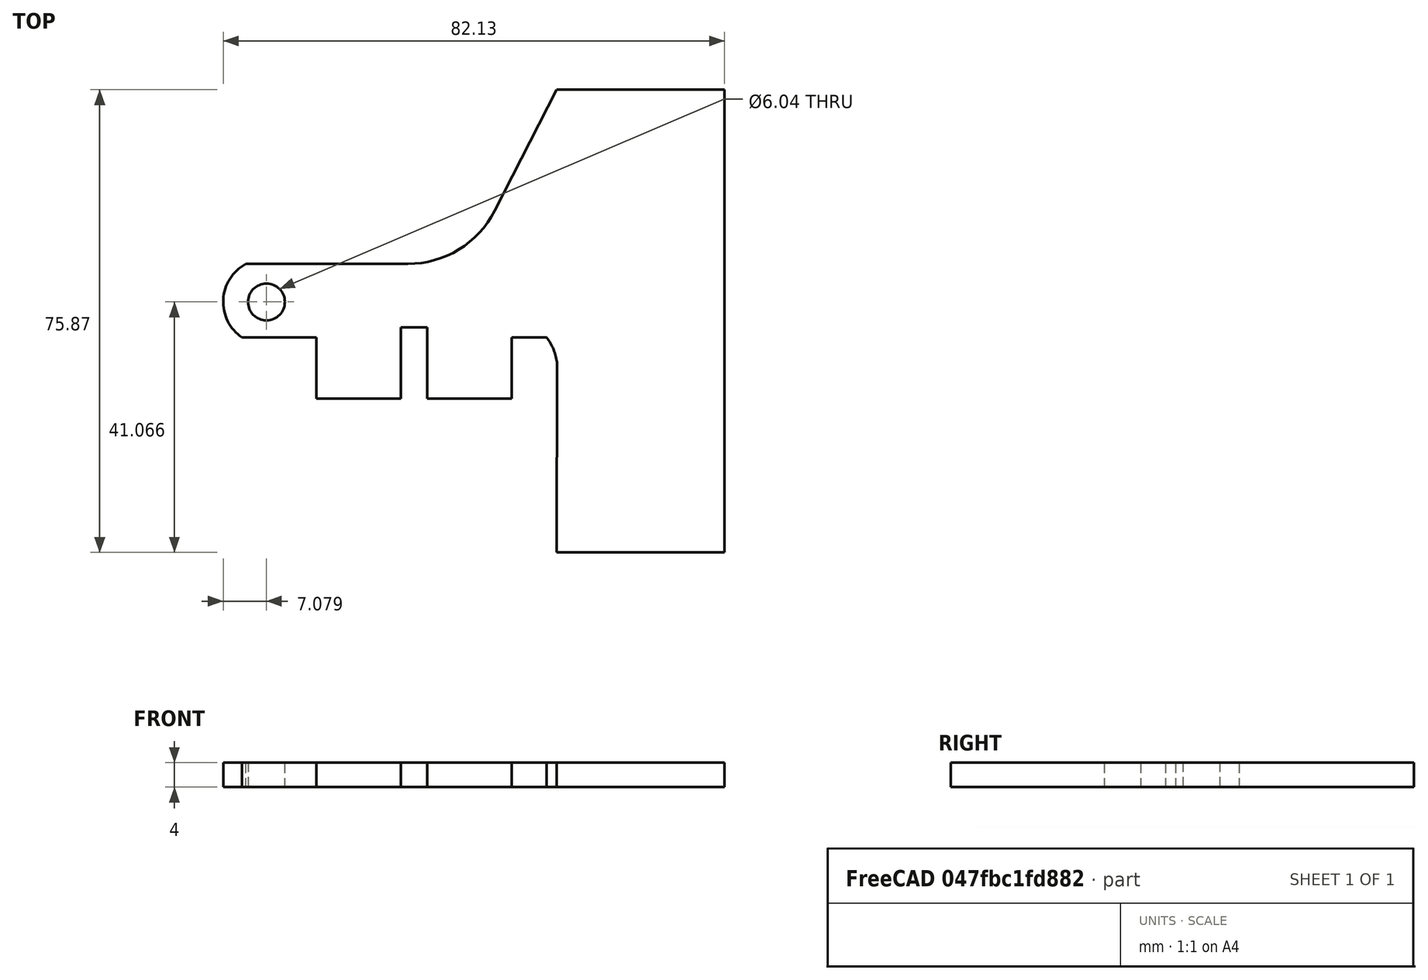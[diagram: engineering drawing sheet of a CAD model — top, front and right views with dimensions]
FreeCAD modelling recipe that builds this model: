
FCSTD DOCUMENT  (FreeCAD 0.18R16131 (Git))
Label: solo_banderuola4mm_v3
License: All rights reserved
LicenseURL: http://en.wikipedia.org/wiki/All_rights_reserved
objects: Sketcher::SketchObject×1, PartDesign::Pad×1, PartDesign::Body×1
note: 4 computed .brp shape members not serialized (recipe doc carries the construction recipe); baked Part::Feature solids carry a one-line shape summary decoded from their .brp

FEATURE [Sketcher::SketchObject] CopySketch004
  sketch-geometry (24):
    g0: LineSegment StartX=-27.5345 StartY=12.0853 StartZ=0 EndX=-1.01073 EndY=12.0853 EndZ=0
    g1: LineSegment StartX=13.2094 StartY=20.7802 StartZ=0 EndX=23.3838 EndY=40.6518 EndZ=0
    g2: LineSegment StartX=23.3838 StartY=40.6518 StartZ=0 EndX=50.8604 EndY=40.6518 EndZ=0
    g3: LineSegment StartX=50.8604 StartY=40.6518 StartZ=0 EndX=50.8604 EndY=0 EndZ=0
    g4: ArcOfCircle CenterX=-1.01073 CenterY=28.061 CenterZ=0 NormalX=0 NormalY=0 NormalZ=1 AngleXU=0 Radius=15.9757 StartAngle=4.71239 EndAngle=5.80998
    g5: GeomPoint X=16 Y=0 Z=0
    g6: GeomPoint X=-16 Y=-9e-16 Z=0
    g7: LineSegment StartX=-16 StartY=-9e-16 StartZ=0 EndX=-16 EndY=-10 EndZ=0
    g8: LineSegment StartX=-16 StartY=-10 StartZ=0 EndX=-2.15 EndY=-10 EndZ=0
    g9: LineSegment StartX=16 StartY=-10 StartZ=0 EndX=16 EndY=0 EndZ=0
    g10: GeomPoint X=-2.15 Y=-10 Z=0
    g11: GeomPoint X=2.15 Y=-10 Z=0
    g12: LineSegment StartX=-2.15 StartY=-10 StartZ=0 EndX=-2.15 EndY=1.64739 EndZ=0
    g13: LineSegment StartX=-2.15 StartY=1.64739 StartZ=0 EndX=2.15 EndY=1.64739 EndZ=0
    g14: LineSegment StartX=2.15 StartY=1.64739 StartZ=0 EndX=2.15 EndY=-10 EndZ=0
    g15: LineSegment StartX=2.15 StartY=-10 StartZ=0 EndX=16 EndY=-10 EndZ=0
    g16: ArcOfCircle CenterX=15.5785 CenterY=-4.94395 CenterZ=0 NormalX=0 NormalY=0 NormalZ=1 AngleXU=0 Radius=7.87288 StartAngle=0.112427 EndAngle=0.678944
    g17: LineSegment StartX=23.4017 StartY=-4.06069 StartZ=0 EndX=23.3838 EndY=-35.221 EndZ=0
    g18: LineSegment StartX=23.3838 StartY=-35.221 StartZ=0 EndX=50.8604 EndY=-35.221 EndZ=0
    g19: LineSegment StartX=50.8604 StartY=-35.221 StartZ=0 EndX=50.8604 EndY=0 EndZ=0
    g20: LineSegment StartX=16 StartY=0 StartZ=0 EndX=21.7055 EndY=0 EndZ=0
    g21: LineSegment StartX=-16 StartY=-9e-16 StartZ=0 EndX=-28.1836 EndY=-9e-16 EndZ=0
    g22: Circle CenterX=-24.1906 CenterY=5.84561 CenterZ=0 NormalX=0 NormalY=0 NormalZ=1 AngleXU=0 Radius=3.02
    g23: ArcOfCircle CenterX=-24.1906 CenterY=5.84561 CenterZ=0 NormalX=0 NormalY=0 NormalZ=1 AngleXU=0 Radius=7.07922 StartAngle=2.06276 EndAngle=4.11311
  constraints (48):
    c: Horizontal(g0)
    c: Coincident(g1,g2)
    c: Horizontal(g2)
    c: Coincident(g2,g3)
    c: PointOnObject(g3,g-1)
    c: Vertical(g3)
    c: Tangent(g0,g4) = -1.5708
    c: Tangent(g1,g4) = -1.5708
    c: DistanceX(g6,g5) = 32
    c: Symmetric(g5,g6,g-2)
    c: Coincident(g7,g6)
    c: Vertical(g7)
    c: Coincident(g7,g8)
    c: Horizontal(g8)
    c: Coincident(g15,g9)
    c: Vertical(g9)
    c: Coincident(g9,g5)
    c: PointOnObject(g10,g8)
    c: DistanceY(g9,g9) = 10
    c: Symmetric(g10,g11,g-2)
    c: Coincident(g12,g10)
    c: Vertical(g12)
    c: Coincident(g12,g13)
    c: Horizontal(g13)
    c: Coincident(g13,g14)
    c: Coincident(g14,g11)
    c: Vertical(g14)
    c: PointOnObject(g8,g12)
    c: PointOnObject(g15,g14)
    c: Tangent(g8,g15)
    c: DistanceX(g8,g11) = 4.3
    c: Coincident(g17,g18)
    c: Horizontal(g18)
    c: Coincident(g18,g19)
    c: Vertical(g19)
    c: PointOnObject(g5,g-1)
    c: Equal(g2,g18)
    c: Coincident(g19,g3)
    c: Coincident(g20,g5)
    c: Horizontal(g20)
    c: Coincident(g17,g16)
    c: Coincident(g21,g6)
    c: Horizontal(g21)
    c: Coincident(g16,g20)
    c: Radius(g22) = 3.02
    c: Coincident(g23,g22)
    c: Coincident(g23,g0)
    c: Coincident(g23,g21)
FEATURE [PartDesign::Pad] Pad
  Length = 4
  Length2 = 100
  Midplane = true
  Profile = -> CopySketch004
  Type = 0
FEATURE [PartDesign::Body] Body001
  Group = -> [Pad]
  Origin = -> Origin001
  Tip = -> Pad
